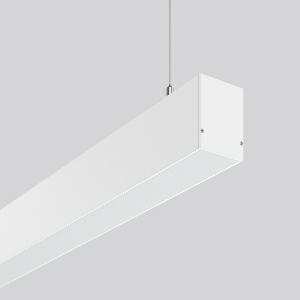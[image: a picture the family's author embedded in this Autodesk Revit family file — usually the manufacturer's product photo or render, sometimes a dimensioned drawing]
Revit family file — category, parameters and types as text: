
# Revit family: less_is_more_50_312319_002_1_7ad6
name_source: partatom
category: Lighting Fixtures
units: mm (PartAtom-declared; Revit-internal decimal feet)

## family parameters
Cut with Voids When Loaded = No
Host = Face
Light Source = No
Part Type = Normal
Room Calculation Point = No
Round Connector Dimension = Use Diameter
Shared = No

## types (1)
- LESS IS MORE 50 (1 x LED Modul 840, 6450 lm, 4000)
    Apparent Load = 52 VA
    CIE Flux Codes = 49 80 96 63 100
    Color Rendering = 80
    Color Temperature = 4000
    Default Elevation = 1800 mm
    Description = Series: LESS IS MORE 50
Linear pendant luminaire for aesthetically sophisticated lighting. Housing: extruded aluminium profile, powder-coated. End cap aluminium powder-coated. Canopy made of aluminium, powder-coated. Diffuser made of non-yellowing plastic (PMMA), opal. Direct 65%, indirect 35% light emission. Suitable for pendant. 2-point steel cable suspension freely positionable and infinitely height-adjustable. Special lengths available on request. LED unit with integrated converter interchangeable and removable. Suitable for through-wiring. With sensors or as a safety luminaire on request. 
Colour: traffic white, matt (RAL 9016)
Length: 1407 mm
Width: 57 mm
Height: 75 mm
Suspension length: 2000 mm
Lamp: LED
Socket: without socket
Colour temperature: 4000K
Colour rendering index (CRI): 80
Light source: LED
Socket lamp2: Without base
Colour temperature: 4000K
System power: 52 W
Rated luminous flux: 6450 lm
Luminous efficiency: 124 lm/W
Control gear: Regulated power supply
Control gear: Regulated power supply
Protection class: I
Type of protection: IP 20
    Height = 75 mm
    Lamp = 1 x LED Modul 840
    Lamp Light Flux = 6450 lm
    Lamp count = 1
    Length = 1407 mm
    Lifetime = 50000 h
    Luminous efficacy = 124 lm/W
    Manufacturer = RZB
    ModVariant = No
    Model = 312319.002.1
    Mounting Place = Ceiling
    Mounting Type = Pendant
    Number of Poles = 1
    OnlyDefault = Yes
    Power Factor = 1
    Product Name = LESS IS MORE 50
    Product group = Pendant LED linear luminaires
    ProductGroupID = 907
    Protection Class = Protection class I
    Protection Degree = IP 20
    RLX_Detail_Level = 1
    RLX_Emergency_Light_Flux = 0 lm
    RLX_Emergency_Type = 0
    RLX_Emergency_Type_DB = No
    RlxData = <blob elided: 31617 chars, md5=145270ee>
    Socket = socket
    Standby Power = 0 W
    System Light Flux = 6450 lm
    System Power = 52 W
    Type Comments = Product without accessories
    Type Image = 312318.002.jpg
    URL = http://relux.com
    VarID = ---
    Voltage = 230 V
    Voltage Range = 220-240 V
    Weight = 0.00 kg
    Width = 57 mm

## geometry (parser evidence)
native form markers: Blend x4, Sweep x13
no freeform markers — native parametric forms only
